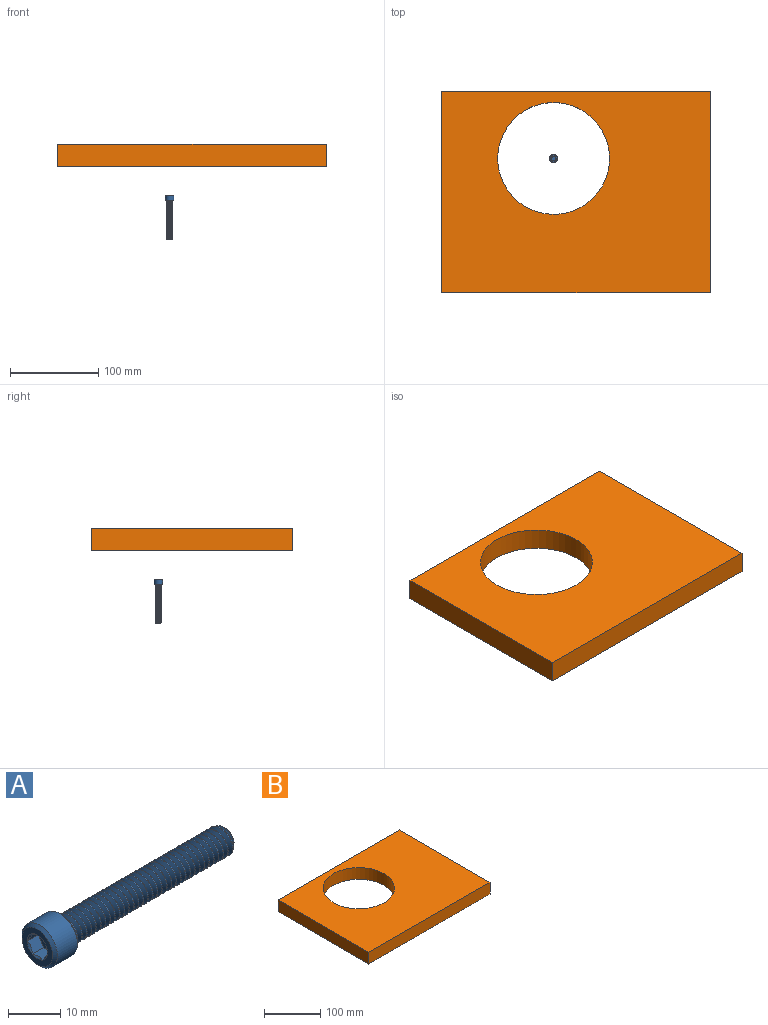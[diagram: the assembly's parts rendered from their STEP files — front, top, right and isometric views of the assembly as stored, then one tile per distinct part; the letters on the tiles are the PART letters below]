
ASSEMBLY  parts=2 mates=1
PART A: 25 faces, bbox 52.2x10.6x10.6 mm
  f0: cone r=4.45mm half-angle=45deg, axis (-1,0,0), area 13mm2, adj f2,f11
  f1: cone r=4.76mm half-angle=45deg, axis (1,0,0), area 25.1mm2, adj f2,f6
  f2: cylinder r=4.76mm len=9.53mm, axis (1,0,0), area 161.5mm2, adj f0,f1
  f3: cone r=2.22mm half-angle=45deg, axis (-1,0,0), area 12.2mm2, adj f4,f5,f7,f8,f9,f10
  f4: cone r=2.22mm half-angle=45deg, axis (-1,0,0), area 0.2mm2, adj f3,f5,f10
  f5: cylinder r=3.17mm len=43.5mm, axis (1,0,0), area 108.5mm2, adj f3,f4,f8,f10,f11
  f6: plane 8.26x8.26mm, normal (-1,0,0), area 29.8mm2, adj f1,f12,f13,f14,f15,f16,f17
  f7: plane 4.45x4.45mm, normal (1,0,0), area 15.5mm2, adj f3
  f8: bspline ~45.28x6.34mm, area 572.5mm2, adj f3,f5,f9,f11
  f9: bspline ~44.64x4.63mm, area 81.7mm2, adj f3,f8,f10,f11
  f10: bspline ~44.8x6.35mm, area 572mm2, adj f3,f4,f5,f9,f11
  f11: plane 9.38x9.38mm, normal (1,0,0), area 37.8mm2, adj f0,f5,f8,f9,f10
  f12: cone r=2.75mm half-angle=45deg, axis (-1,0,0), area 0mm2, adj f6,f19
  f13: cone r=2.75mm half-angle=45deg, axis (-1,0,0), area 0mm2, adj f6,f20
  f14: cone r=2.75mm half-angle=45deg, axis (-1,0,0), area 0mm2, adj f6,f21
  f15: cone r=2.75mm half-angle=45deg, axis (-1,0,0), area 0mm2, adj f6,f22
  f16: cone r=2.75mm half-angle=45deg, axis (-1,0,0), area 0mm2, adj f6,f23
  f17: cone r=2.75mm half-angle=45deg, axis (-1,0,0), area 0mm2, adj f6,f24
  f18: plane 5.5x4.76mm, normal (-1,0,0), area 19.6mm2, adj f19,f20,f21,f22,f23,f24
  f19: plane 4.09x3.79mm, normal (0,0,1), area 7.7mm2, adj f12,f18,f20,f24
  f20: plane 4.09x3.42mm, normal (0,0.87,0.5), area 7.7mm2, adj f13,f18,f19,f21
  f21: plane 4.09x3.42mm, normal (0,0.87,-0.5), area 7.7mm2, adj f14,f18,f20,f22
  f22: plane 4.09x3.79mm, normal (0,0,-1), area 7.7mm2, adj f15,f18,f21,f23
  f23: plane 4.09x3.42mm, normal (0,-0.87,-0.5), area 7.7mm2, adj f16,f18,f22,f24
  f24: plane 4.09x3.42mm, normal (0,-0.87,0.5), area 7.7mm2, adj f17,f18,f19,f23
PART B: 7 faces, bbox 304.8x228.6x25.4 mm
  f0: plane 304.8x25.4mm, normal (0,1,0), area 7741.9mm2, adj f1,f4,f5,f6
  f1: plane 228.6x25.4mm, normal (-1,0,0), area 5806.4mm2, adj f0,f2,f5,f6
  f2: plane 304.8x25.4mm, normal (0,-1,0), area 7741.9mm2, adj f1,f4,f5,f6
  f3: cylinder r=63.5mm len=127mm, axis (0,0,-1), area 10134.1mm2, adj f5,f6
  f4: plane 228.6x25.4mm, normal (1,0,0), area 5806.4mm2, adj f0,f2,f5,f6
  f5: plane 304.8x228.6mm, normal (0,0,1), area 57009.6mm2, adj f0,f1,f2,f3,f4
  f6: plane 304.8x228.6mm, normal (0,0,-1), area 57009.6mm2, adj f0,f1,f2,f3,f4
PLACE A rot(axis=(0,1,0),90deg) t=(79.88,94.51,4.68)mm
PLACE B t=(-47.12,-57.89,78.74)mm
MATE cylindrical A.f2 <-> B.f3  axis (0,0,-1) through (79.88,94.51,29.92)mm
